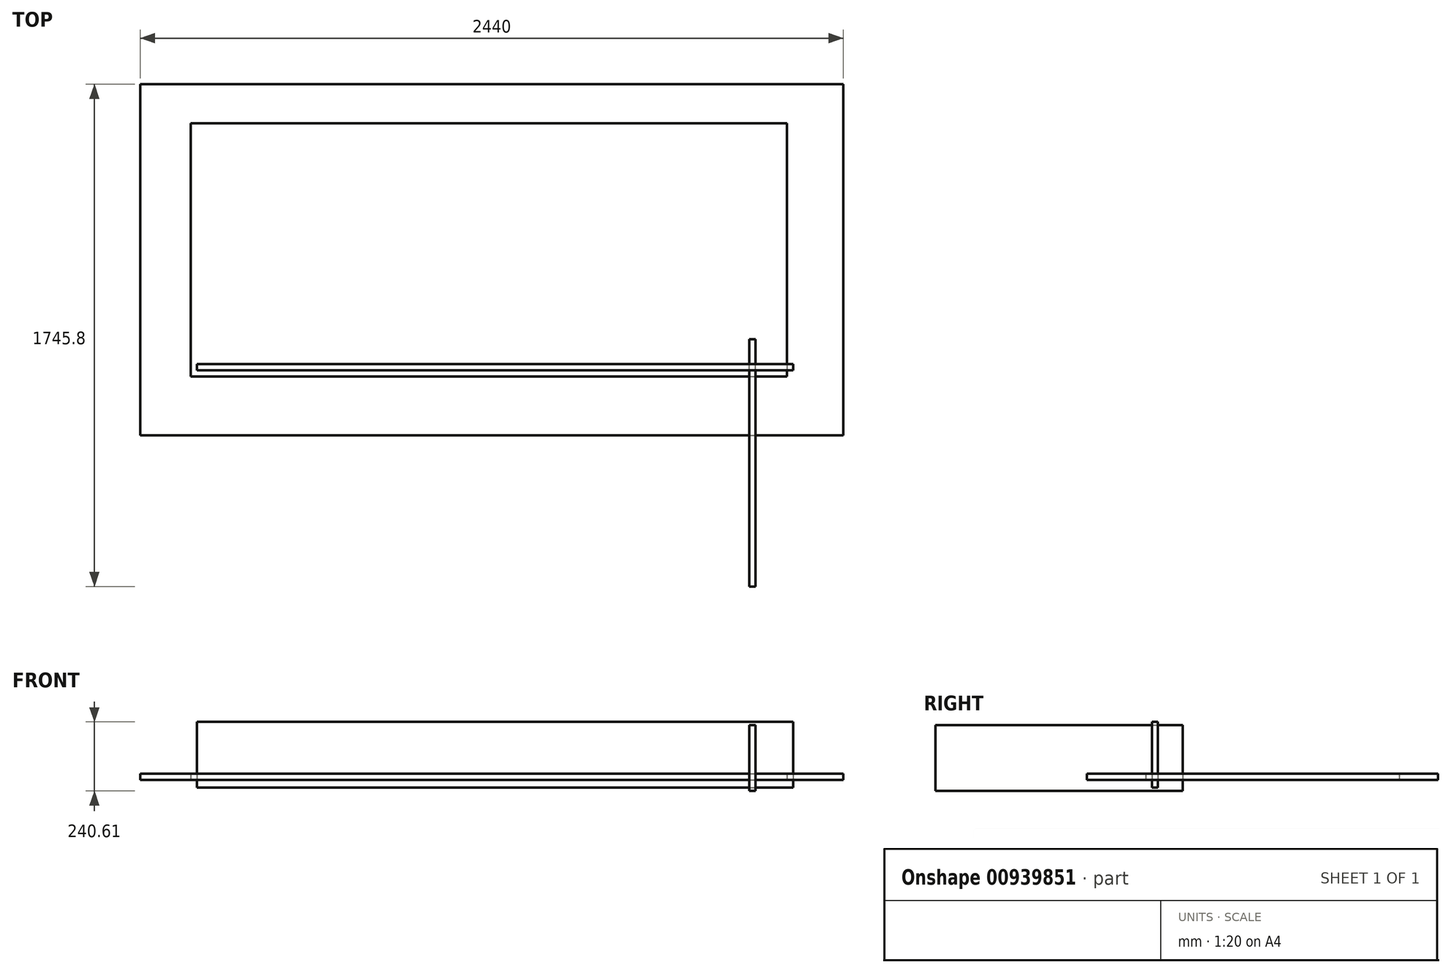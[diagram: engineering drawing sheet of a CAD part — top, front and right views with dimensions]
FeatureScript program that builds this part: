
annotation { "Feature Type Name" : "Feature", "Feature Type Description" : "" }
export const myFeature = defineFeature(function(context is Context, id is Id, definition is map)
    precondition{}
    {
        {
            var Q0;
            Q0=qCreatedBy(makeId("Top.planeOp"),FACE);
            var sketch = newSketch(context, id + "F0", { "sketchPlane" : qUnion([Q0])});
            skLineSegment(sketch, "E0.bottom", {"start": v(-1940.03, 837.81) * mm, "end": v(129.97, 837.81) * mm});
            skLineSegment(sketch, "E0.top", {"start": v(-1940.03, -42.19) * mm, "end": v(129.97, -42.19) * mm});
            skLineSegment(sketch, "E0.left", {"start": v(-1940.03, 837.81) * mm, "end": v(-1940.03, -42.19) * mm});
            skLineSegment(sketch, "E0.right", {"start": v(129.97, 837.81) * mm, "end": v(129.97, -42.19) * mm});
            skSolve(sketch);
        }
        {
            var Q0;
            Q0=qSketchRegion(id+"F0",true);
            extrude(context, id + "F1", {"entities" : qUnion([Q0]), "depth" : 21 * mm, "offsetDistance" : 25 * mm});
        }
        {
            var Q0;
            Q0=qCreatedBy(makeId("Front.planeOp"),FACE);
            var sketch = newSketch(context, id + "F2", { "sketchPlane" : qUnion([Q0])});
            skLineSegment(sketch, "E1.bottom", {"start": v(-1917.71, 201.51) * mm, "end": v(152.29, 201.51) * mm});
            skLineSegment(sketch, "E1.top", {"start": v(-1917.71, -27.49) * mm, "end": v(152.29, -27.49) * mm});
            skLineSegment(sketch, "E1.left", {"start": v(-1917.71, 201.51) * mm, "end": v(-1917.71, -27.49) * mm});
            skLineSegment(sketch, "E1.right", {"start": v(152.29, 201.51) * mm, "end": v(152.29, -27.49) * mm});
            skSolve(sketch);
        }
        {
            var Q0;
            Q0=qSketchRegion(id+"F2",true);
            extrude(context, id + "F3", {"entities" : qUnion([Q0]), "depth" : 21 * mm, "offsetDistance" : 25 * mm});
        }
        {
            var Q0;
            Q0=qCreatedBy(makeId("Right.planeOp"),FACE);
            var sketch = newSketch(context, id + "F4", { "sketchPlane" : qUnion([Q0])});
            skLineSegment(sketch, "E2.bottom", {"start": v(-772.75, 189.9) * mm, "end": v(86.25, 189.9) * mm});
            skLineSegment(sketch, "E2.top", {"start": v(-772.75, -39.1) * mm, "end": v(86.25, -39.1) * mm});
            skLineSegment(sketch, "E2.left", {"start": v(-772.75, 189.9) * mm, "end": v(-772.75, -39.1) * mm});
            skLineSegment(sketch, "E2.right", {"start": v(86.25, 189.9) * mm, "end": v(86.25, -39.1) * mm});
            skSolve(sketch);
        }
        {
            var Q0;
            Q0=qSketchRegion(id+"F4",true);
            extrude(context, id + "F5", {"entities" : qUnion([Q0]), "depth" : 21 * mm, "offsetDistance" : 25 * mm});
        }
        {
            var Q0;
            Q0=qCreatedBy(makeId("Top.planeOp"),FACE);
            var sketch = newSketch(context, id + "F6", { "sketchPlane" : qUnion([Q0])});
            skLineSegment(sketch, "E3.bottom", {"start": v(-2114.14, 973.05) * mm, "end": v(325.86, 973.05) * mm});
            skLineSegment(sketch, "E3.top", {"start": v(-2114.14, -246.95) * mm, "end": v(325.86, -246.95) * mm});
            skLineSegment(sketch, "E3.left", {"start": v(-2114.14, 973.05) * mm, "end": v(-2114.14, -246.95) * mm});
            skLineSegment(sketch, "E3.right", {"start": v(325.86, 973.05) * mm, "end": v(325.86, -246.95) * mm});
            skSolve(sketch);
        }
        {
            var Q0;
            Q0 = qSketchRegion(id + "F6", true);
            extrude(context, id + "F7", {"entities" : qUnion([Q0]), "depth" : 21 * mm, "offsetDistance" : 25 * mm});
        }
    });
